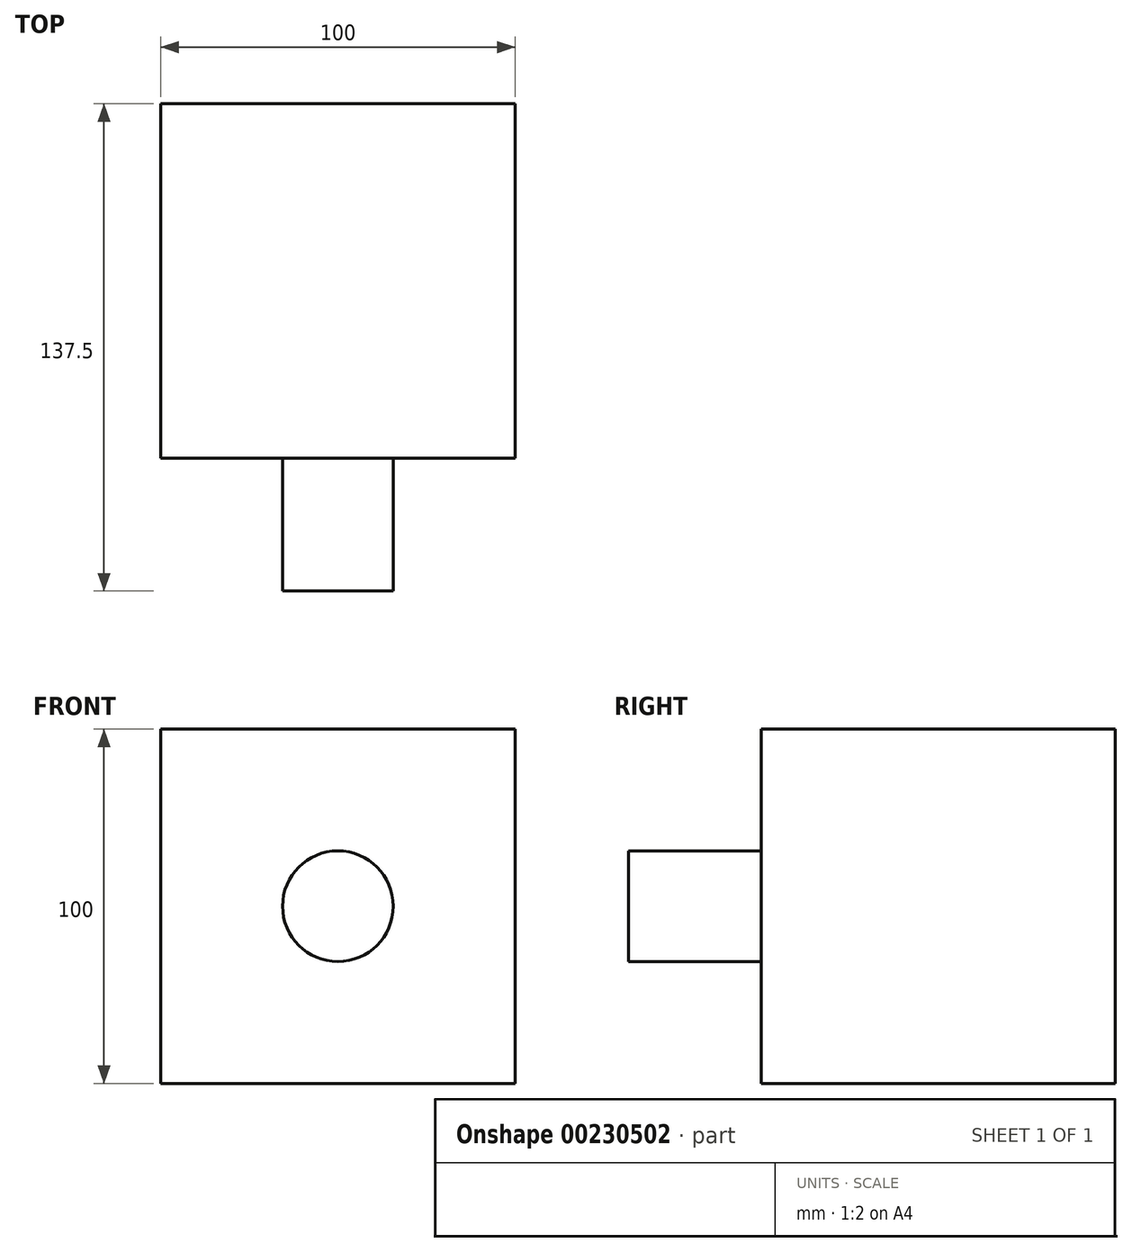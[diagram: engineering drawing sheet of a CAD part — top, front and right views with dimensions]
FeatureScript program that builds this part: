
annotation { "Feature Type Name" : "Feature", "Feature Type Description" : "" }
export const myFeature = defineFeature(function(context is Context, id is Id, definition is map)
    precondition{}
    {
        {
            var Q0;
            Q0=qCreatedBy(makeId("Front.planeOp"),FACE);
            var sketch = newSketch(context, id + "F0", { "sketchPlane" : qUnion([Q0])});
            skLineSegment(sketch, "E0.bottom", {"start": v(-50, 50) * mm, "end": v(50, 50) * mm});
            skLineSegment(sketch, "E0.top", {"start": v(-50, -50) * mm, "end": v(50, -50) * mm});
            skLineSegment(sketch, "E0.left", {"start": v(-50, 50) * mm, "end": v(-50, -50) * mm});
            skLineSegment(sketch, "E0.right", {"start": v(50, 50) * mm, "end": v(50, -50) * mm});
            skSolve(sketch);
        }
        {
            var Q0;
            Q0=makeQuery(id+"F0.imprint","IMPRINT",FACE,{"disambiguationData":[TD([[makeQuery(id+"F0.imprint","IMPRINT",EDGE,{"derivedFrom":sQuery(id+"F0.wireOp",EDGE,"E0.bottom")}),-1.0]])]});
            extrude(context, id + "F1", {"entities" : qUnion([Q0]), "endBound" : BoundingType.SYMMETRIC, "depth" : 100 * mm});
        }
        {
            var Q0;
            Q0=makeQuery(id+"F1.opExtrude","CAP_FACE",FACE,{"disambiguationData":[OSD([sQuery(id+"F0.wireOp",EDGE,"E0.bottom"),sQuery(id+"F0.wireOp",EDGE,"E0.top"),sQuery(id+"F0.wireOp",EDGE,"E0.left"),sQuery(id+"F0.wireOp",EDGE,"E0.right")])],"isStart":false});
            var sketch = newSketch(context, id + "F2", { "sketchPlane" : qUnion([Q0])});
            skCircle(sketch, "E1", {"center": v(0, 0) * mm, "radius": 15.62 * mm});
            skCircle(sketch, "E2", {"center": v(0, 0) * mm, "radius": 31.25 * mm});
            skCircle(sketch, "E3", {"center": v(0, 0) * mm, "radius": 46.88 * mm});
            skSolve(sketch);
        }
        {
            var Q0;
            Q0=makeQuery(id+"F2.imprint","IMPRINT",FACE,{"disambiguationData":[TD([[makeQuery(id+"F2.imprint","IMPRINT",EDGE,{"derivedFrom":sQuery(id+"F2.wireOp",EDGE,"E1")}),1.0]])]});
            extrude(context, id + "F3", {"entities" : qUnion([Q0]), "operationType" : NewBodyOperationType.ADD, "endBound" : BoundingType.SYMMETRIC, "oppositeDirection" : true, "depth" : 75 * mm});
        }
        {
            var Q0;
            Q0=makeQuery(id+"F2.imprint","IMPRINT",FACE,{"disambiguationData":[TD([[makeQuery(id+"F2.imprint","IMPRINT",EDGE,{"derivedFrom":sQuery(id+"F2.wireOp",EDGE,"E1")}),-1.0]])]});
            extrude(context, id + "F4", {"entities" : qUnion([Q0]), "operationType" : NewBodyOperationType.ADD, "oppositeDirection" : true, "depth" : 50 * mm});
        }
    });
